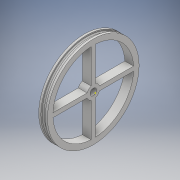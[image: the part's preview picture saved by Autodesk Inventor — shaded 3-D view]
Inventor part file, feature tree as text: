
AUTODESK INVENTOR PART (.ipt)
format: ipt  version: 2018 (Build 220112000, 112)  size: 374,784 bytes
history: native  units: mm
features: sketch x11, extrude x10, fillet x1, pattern_circular x1
ambient origin geometry x8: Origin, YZ Plane, XZ Plane, XY Plane, X Axis, Y Axis, Z Axis, Center Point
bodies: Solid1 (feature_tree)
feature tree (23):
  extrude  "Extrusion1"  Depth=5.0mm TaperAngle=0.0deg
  extrude  "Extrusion2"  Depth=2.0mm TaperAngle=0.0deg
  extrude  "Extrusion3"  Depth=0.5mm
  fillet  "Fillet1"  Radius=37.0mm
  extrude  "Extrusion4"  Depth=4.0mm
  extrude  "Extrusion5"  Depth=6.0mm TaperAngle=0.0deg
  sketch  "Sketch6"  dims[d16=1.0mm d17=0.0mm d18=1.0mm d19=0.0mm]
  sketch  "Sketch7"  dims[d20=1.0mm d21=0.0mm d22=1.0mm]
  extrude  "Extrusion6"  Depth=1.0mm TaperAngle=0.0deg
  extrude  "Extrusion7"  Depth=1.0mm
  extrude  "Extrusion8"  Depth=2.0mm
  extrude  "Extrusion9"  Depth=4.0mm TaperAngle=360.0deg
  pattern_circular  "Circular Pattern1"  [2 undecoded]
  extrude  "Extrusion10"  [1 undecoded]
  sketch  "Sketch1"  dims[d0=40.0mm d1=5.0mm d2=0.0mm]
  sketch  "Sketch2"  dims[d3=42.0mm d4=2.0mm d5=0.0mm]
  sketch  "Sketch3"  dims[d6=2.0mm d7=0.0mm d8=0.5mm d9=37.0mm]
  sketch  "Sketch4"  dims[d10=6.0mm d11=0.0mm d12=4.0mm]
  sketch  "Sketch5"  dims[d13=6.0mm d14=6.0mm d15=0.0mm]
  sketch  "Sketch8"  dims[d23=2.0mm d24=2.0mm]
  sketch  "Sketch9"  dims[d25=4.0mm d26=0.0mm d27=40.0mm d28=360.0deg]
  sketch  "Sketch10"  dims[d30=3.0mm]
  sketch  "Sketch11"  dims[d31=4.0mm d32=0.0mm]
note: 3 required parameter values undecoded (feature->parameter linkage not recoverable at this tier; creation-order binding heuristic only, values carry confidence <= 0.55)
